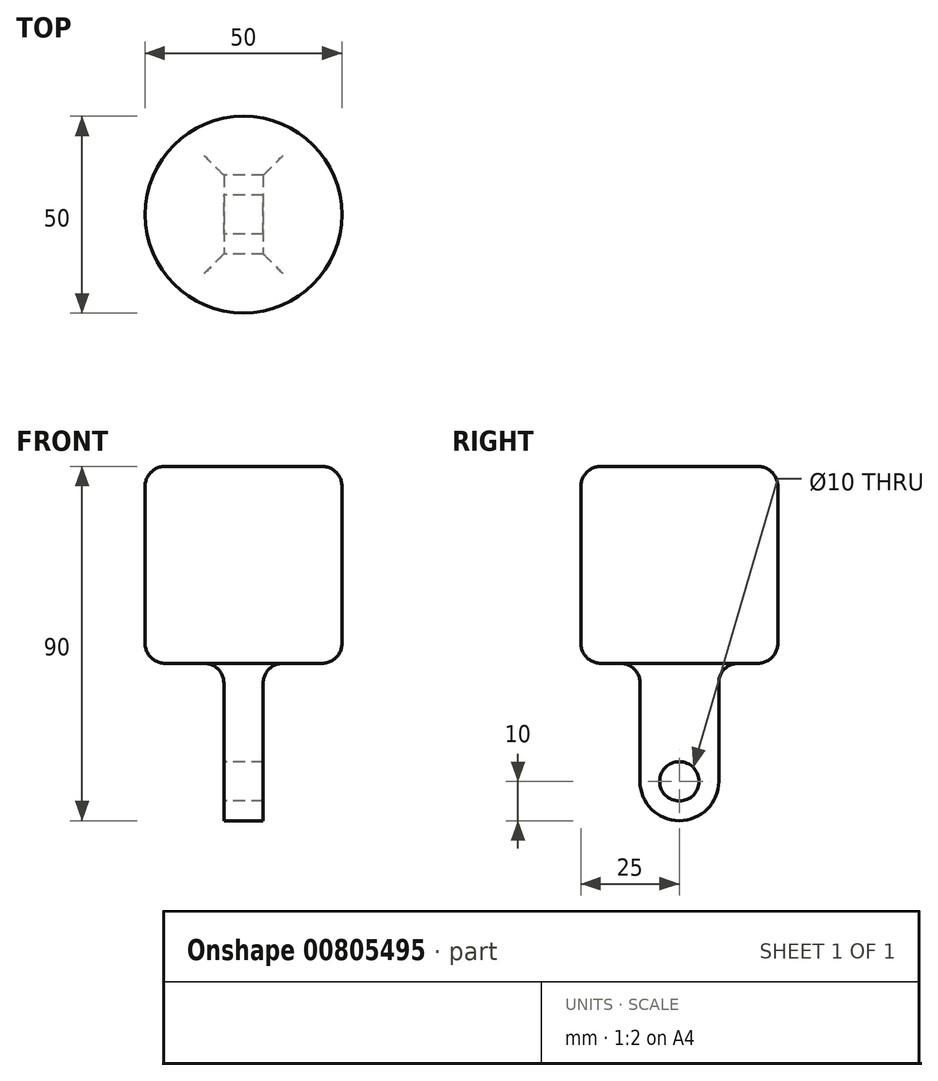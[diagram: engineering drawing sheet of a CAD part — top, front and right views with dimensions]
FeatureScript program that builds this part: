
annotation { "Feature Type Name" : "Feature", "Feature Type Description" : "" }
export const myFeature = defineFeature(function(context is Context, id is Id, definition is map)
    precondition{}
    {
        {
            var Q0;
            Q0=qCreatedBy(makeId("Top.planeOp"),FACE);
            var sketch = newSketch(context, id + "F0", { "sketchPlane" : qUnion([Q0])});
            skCircle(sketch, "E0", {"center": v(0, 0) * mm, "radius": 25 * mm});
            skSolve(sketch);
        }
        {
            var Q0;
            Q0=makeQuery(id+"F0.imprint","IMPRINT",FACE,{"disambiguationData":[TD([[makeQuery(id+"F0.imprint","IMPRINT",EDGE,{"derivedFrom":sQuery(id+"F0.wireOp",EDGE,"E0")}),1.0]])]});
            extrude(context, id + "F1", {"entities" : qUnion([Q0]), "depth" : 50 * mm});
        }
        {
            var Q0;
            Q0=makeQuery(id+"F1.opExtrude","CAP_FACE",FACE,{"disambiguationData":[OSD([sQuery(id+"F0.wireOp",EDGE,"E0")])],"isStart":true});
            var sketch = newSketch(context, id + "F2", { "sketchPlane" : qUnion([Q0])});
            skLineSegment(sketch, "E1.bottom", {"start": v(5, -10) * mm, "end": v(-5, -10) * mm});
            skLineSegment(sketch, "E1.top", {"start": v(5, 10) * mm, "end": v(-5, 10) * mm});
            skLineSegment(sketch, "E1.left", {"start": v(5, -10) * mm, "end": v(5, 10) * mm});
            skLineSegment(sketch, "E1.right", {"start": v(-5, -10) * mm, "end": v(-5, 10) * mm});
            skPoint(sketch, "E1.middle", {"position": v(0, 0) * mm});
            skSolve(sketch);
        }
        {
            var Q0;
            Q0=makeQuery(id+"F2.imprint","IMPRINT",FACE,{"disambiguationData":[TD([[makeQuery(id+"F2.imprint","IMPRINT",EDGE,{"derivedFrom":sQuery(id+"F2.wireOp",EDGE,"E1.bottom")}),-1.0]])]});
            extrude(context, id + "F3", {"entities" : qUnion([Q0]), "operationType" : NewBodyOperationType.ADD, "depth" : 40 * mm});
        }
        {
            var Q0;
            Q0=makeQuery(id+"F3.opExtrude","CAP_EDGE",EDGE,{"disambiguationData":[OSD([sQuery(id+"F2.wireOp",EDGE,"E1.bottom")])],"isStart":false});
            var Q1;
            Q1=makeQuery(id+"F3.opExtrude","CAP_EDGE",EDGE,{"disambiguationData":[OSD([sQuery(id+"F2.wireOp",EDGE,"E1.top")])],"isStart":false});
            fillet(context, id + "F6", {"entities" : qUnion([Q0, Q1]), "radius" : 10 * mm, "tangentPropagation" : true, "allowEdgeOverflow" : false});
        }
        {
            var Q0;
            Q0=makeQuery(id+"F1.opExtrude","CAP_EDGE",EDGE,{"disambiguationData":[OSD([sQuery(id+"F0.wireOp",EDGE,"E0")])],"isStart":false});
            var Q1;
            Q1=makeQuery(id+"F1.opExtrude","CAP_FACE",FACE,{"disambiguationData":[OSD([sQuery(id+"F0.wireOp",EDGE,"E0")])],"isStart":true});
            fillet(context, id + "F7", {"entities" : qUnion([Q0, Q1]), "radius" : 5 * mm, "tangentPropagation" : true, "allowEdgeOverflow" : false});
        }
        {
            var Q0;
            Q0=makeQuery(id+"F3.opExtrude","SWEPT_FACE",FACE,{"disambiguationData":[OSD([sQuery(id+"F2.wireOp",EDGE,"E1.right")])]});
            var sketch = newSketch(context, id + "F4", { "sketchPlane" : qUnion([Q0])});
            skPoint(sketch, "E2", {"position": v(0, -30) * mm});
            skSolve(sketch);
        }
        {
            var Q0;
            Q0=sQuery(id+"F4.wireOp",VERTEX,"E2");
            var Q1;
            Q1=makeQuery(id+"F1.opExtrude","SWEPT_BODY",BODY,{"disambiguationData":[OSD([sQuery(id+"F0.wireOp",EDGE,"E0")])]});
            hole(context, id + "F5", {"style" : HoleStyle.SIMPLE, "endStyle" : HoleEndStyle.THROUGH, "holeDiameter" : 10 * mm, "locations" : qUnion([Q0]), "scope" : qUnion([Q1]), "isTappedThrough" : true});
        }
    });
